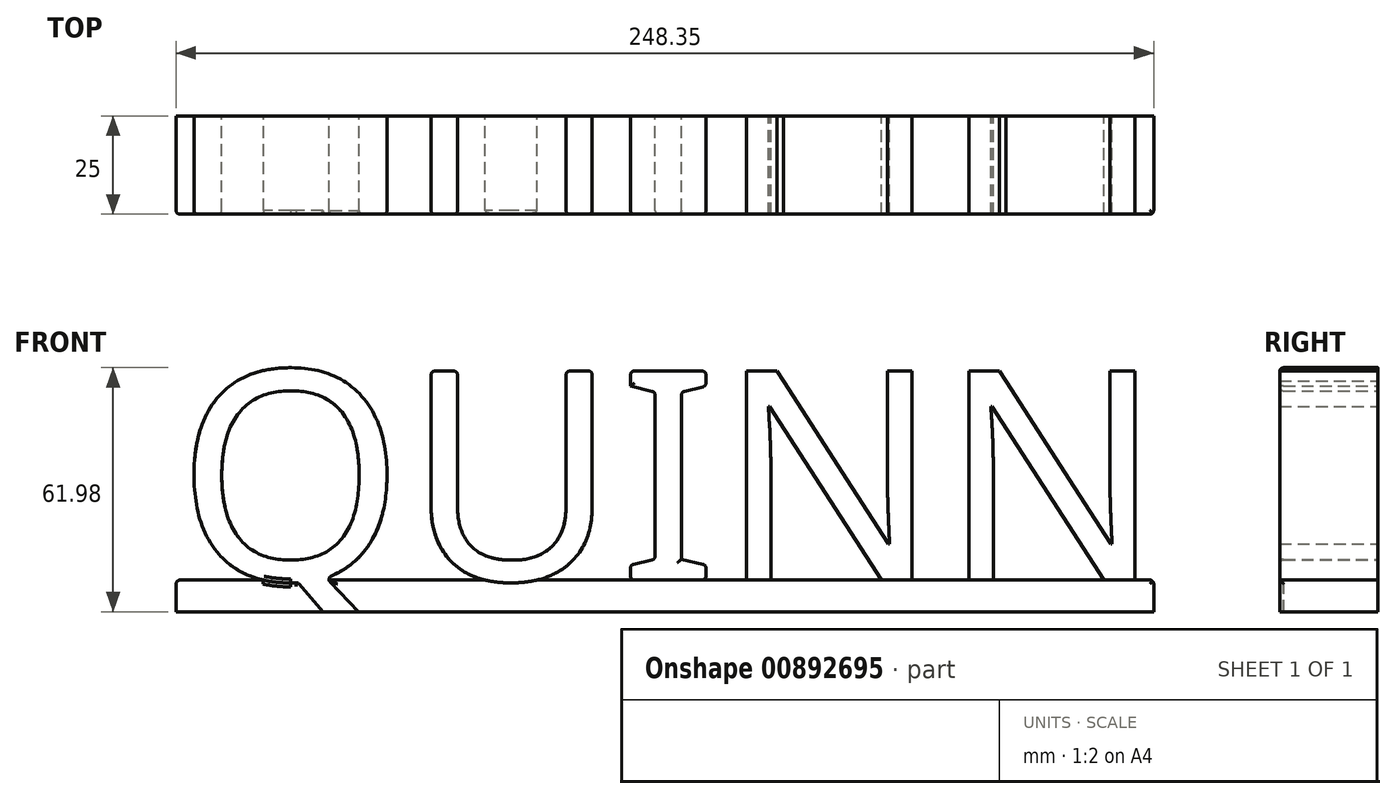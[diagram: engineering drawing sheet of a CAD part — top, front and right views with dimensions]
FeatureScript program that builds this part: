
annotation { "Feature Type Name" : "Feature", "Feature Type Description" : "" }
export const myFeature = defineFeature(function(context is Context, id is Id, definition is map)
    precondition{}
    {
        {
            var Q0;
            Q0=qCreatedBy(makeId("Front.planeOp"),FACE);
            var sketch = newSketch(context, id + "F0", { "sketchPlane" : qUnion([Q0])});
            skText(sketch, "E0", { "text": "QUINN", "fontName": "NotoSans-Regular.ttf"});
            skLineSegment(sketch, "E1.bottom", {"start": v(-74, 3.83) * mm, "end": v(174.35, 3.83) * mm});
            skLineSegment(sketch, "E1.top", {"start": v(-74, -4.21) * mm, "end": v(174.35, -4.21) * mm});
            skLineSegment(sketch, "E1.left", {"start": v(-74, 3.83) * mm, "end": v(-74, -4.21) * mm});
            skLineSegment(sketch, "E1.right", {"start": v(174.35, 3.83) * mm, "end": v(174.35, -4.21) * mm});
            const initialGuessF0  = {"E0": [-0.074, 0.00383, 1, 0, 0.05356]};
            skSetInitialGuess(sketch, initialGuessF0);
            skSolve(sketch);
        }
        {
            var Q0;
            {var subQ1=sQuery(id+"F0.wireOp",EDGE,"E0.sketch_text.stroke-65");Q0=makeQuery(id+"F0.imprint","IMPRINT",FACE,{"disambiguationData":[TD([[makeQuery(id+"F0.imprint","IMPRINT",EDGE,{"derivedFrom":subQ1}),-1.0]])]});}
            var Q1;
            {var subQ2=sQuery(id+"F0.wireOp",EDGE,"E0.sketch_text.stroke-47");Q1=makeQuery(id+"F0.imprint","IMPRINT",FACE,{"disambiguationData":[TD([[makeQuery(id+"F0.imprint","IMPRINT",EDGE,{"derivedFrom":subQ2}),-1.0]])]});}
            var Q2;
            {var subQ0=sQuery(id+"F0.wireOp",EDGE,"E0.sketch_text.stroke-35");Q2=makeQuery(id+"F0.imprint","IMPRINT",FACE,{"disambiguationData":[TD([[makeQuery(id+"F0.imprint","IMPRINT",EDGE,{"derivedFrom":subQ0}),-1.0]])]});}
            var Q3;
            Q3=makeQuery(id+"F0.imprint","IMPRINT",FACE,{"disambiguationData":[TD([[makeQuery(id+"F0.imprint","IMPRINT",EDGE,{"derivedFrom":sQuery(id+"F0.wireOp",EDGE,"E0.sketch_text.stroke-20")}),-1.0]])]});
            var Q4;
            Q4=makeQuery(id+"F0.imprint","IMPRINT",FACE,{"disambiguationData":[TD([[makeQuery(id+"F0.imprint","IMPRINT",EDGE,{"derivedFrom":sQuery(id+"F0.wireOp",EDGE,"E0.sketch_text.stroke-0")}),-1.0]])]});
            var Q5;
            {var subQ1=sQuery(id+"F0.wireOp",EDGE,"E0.sketch_text.stroke-5");Q5=makeQuery(id+"F0.imprint","IMPRINT",FACE,{"disambiguationData":[TD([[makeQuery(id+"F0.imprint","IMPRINT",EDGE,{"derivedFrom":subQ1}),-1.0]])]});}
            var Q6;
            {var subQ0=sQuery(id+"F0.wireOp",EDGE,"E0.sketch_text.stroke-23");var subQ1=sQuery(id+"F0.wireOp",EDGE,"E0.sketch_text.stroke-22");var subQ2=makeQuery(id+"F0.imprint","INTERSECT",VERTEX,{"derivedFrom":[subQ1,subQ0]});Q6=makeQuery(id+"F0.imprint","IMPRINT",FACE,{"disambiguationData":[TD([[makeQuery(id+"F0.imprint","IMPRINT",EDGE,{"disambiguationData":[TD([[subQ2,1.0]])],"derivedFrom":subQ1}),-1.0]])]});}
            extrude(context, id + "F1", {"entities" : qUnion([Q0, Q1, Q2, Q3, Q4, Q5, Q6]), "depth" : 25 * mm, "offsetDistance" : 25 * mm});
        }
        {
            var Q0;
            Q0=makeQuery(id+"F1.opExtrude","CAP_EDGE",EDGE,{"disambiguationData":[OSD([sQuery(id+"F0.wireOp",EDGE,"E0.sketch_text.stroke-7")])],"isStart":false});
            var Q1;
            Q1=makeQuery(id+"F1.opExtrude","CAP_EDGE",EDGE,{"disambiguationData":[OSD([sQuery(id+"F0.wireOp",EDGE,"E0.sketch_text.stroke-14")])],"isStart":false});
            var Q2;
            Q2=makeQuery(id+"F1.opExtrude","CAP_EDGE",EDGE,{"disambiguationData":[OSD([sQuery(id+"F0.wireOp",EDGE,"E0.sketch_text.stroke-2")])],"isStart":false});
            var Q3;
            Q3=makeQuery(id+"F1.opExtrude","CAP_EDGE",EDGE,{"disambiguationData":[OSD([sQuery(id+"F0.wireOp",EDGE,"E0.sketch_text.stroke-4")])],"isStart":false});
            var Q4;
            Q4=makeQuery(id+"F1.opExtrude","CAP_EDGE",EDGE,{"disambiguationData":[OSD([sQuery(id+"F0.wireOp",EDGE,"E0.sketch_text.stroke-5")])],"isStart":false});
            var Q5;
            Q5=makeQuery(id+"F1.opExtrude","CAP_FACE",FACE,{"disambiguationData":[OSD([sQuery(id+"F0.wireOp",EDGE,"E0.sketch_text.stroke-20"),sQuery(id+"F0.wireOp",EDGE,"E0.sketch_text.stroke-21"),sQuery(id+"F0.wireOp",EDGE,"E0.sketch_text.stroke-22"),sQuery(id+"F0.wireOp",EDGE,"E0.sketch_text.stroke-23"),sQuery(id+"F0.wireOp",EDGE,"E0.sketch_text.stroke-24"),sQuery(id+"F0.wireOp",EDGE,"E0.sketch_text.stroke-25"),sQuery(id+"F0.wireOp",EDGE,"E0.sketch_text.stroke-26"),sQuery(id+"F0.wireOp",EDGE,"E0.sketch_text.stroke-27"),sQuery(id+"F0.wireOp",EDGE,"E0.sketch_text.stroke-28"),sQuery(id+"F0.wireOp",EDGE,"E0.sketch_text.stroke-29"),sQuery(id+"F0.wireOp",EDGE,"E0.sketch_text.stroke-30"),sQuery(id+"F0.wireOp",EDGE,"E0.sketch_text.stroke-31"),sQuery(id+"F0.wireOp",EDGE,"E0.sketch_text.stroke-32"),sQuery(id+"F0.wireOp",EDGE,"E0.sketch_text.stroke-33"),sQuery(id+"F0.wireOp",EDGE,"E1.bottom")])],"isStart":false});
            var Q6;
            Q6=makeQuery(id+"F1.opExtrude","CAP_FACE",FACE,{"disambiguationData":[OSD([sQuery(id+"F0.wireOp",EDGE,"E0.sketch_text.stroke-35"),sQuery(id+"F0.wireOp",EDGE,"E0.sketch_text.stroke-36"),sQuery(id+"F0.wireOp",EDGE,"E0.sketch_text.stroke-37"),sQuery(id+"F0.wireOp",EDGE,"E0.sketch_text.stroke-38"),sQuery(id+"F0.wireOp",EDGE,"E0.sketch_text.stroke-39"),sQuery(id+"F0.wireOp",EDGE,"E0.sketch_text.stroke-40"),sQuery(id+"F0.wireOp",EDGE,"E0.sketch_text.stroke-41"),sQuery(id+"F0.wireOp",EDGE,"E0.sketch_text.stroke-42"),sQuery(id+"F0.wireOp",EDGE,"E0.sketch_text.stroke-43"),sQuery(id+"F0.wireOp",EDGE,"E0.sketch_text.stroke-44"),sQuery(id+"F0.wireOp",EDGE,"E0.sketch_text.stroke-45"),sQuery(id+"F0.wireOp",EDGE,"E1.bottom")])],"isStart":false});
            var Q7;
            Q7=makeQuery(id+"F1.opExtrude","CAP_FACE",FACE,{"disambiguationData":[OSD([sQuery(id+"F0.wireOp",EDGE,"E0.sketch_text.stroke-47"),sQuery(id+"F0.wireOp",EDGE,"E0.sketch_text.stroke-48"),sQuery(id+"F0.wireOp",EDGE,"E0.sketch_text.stroke-49"),sQuery(id+"F0.wireOp",EDGE,"E0.sketch_text.stroke-50"),sQuery(id+"F0.wireOp",EDGE,"E0.sketch_text.stroke-51"),sQuery(id+"F0.wireOp",EDGE,"E0.sketch_text.stroke-53"),sQuery(id+"F0.wireOp",EDGE,"E0.sketch_text.stroke-54"),sQuery(id+"F0.wireOp",EDGE,"E0.sketch_text.stroke-55"),sQuery(id+"F0.wireOp",EDGE,"E0.sketch_text.stroke-56"),sQuery(id+"F0.wireOp",EDGE,"E0.sketch_text.stroke-57"),sQuery(id+"F0.wireOp",EDGE,"E0.sketch_text.stroke-58"),sQuery(id+"F0.wireOp",EDGE,"E0.sketch_text.stroke-59"),sQuery(id+"F0.wireOp",EDGE,"E0.sketch_text.stroke-60"),sQuery(id+"F0.wireOp",EDGE,"E0.sketch_text.stroke-61"),sQuery(id+"F0.wireOp",EDGE,"E0.sketch_text.stroke-62"),sQuery(id+"F0.wireOp",EDGE,"E0.sketch_text.stroke-63"),sQuery(id+"F0.wireOp",EDGE,"E1.bottom")])],"isStart":false});
            var Q8;
            Q8=makeQuery(id+"F1.opExtrude","CAP_FACE",FACE,{"disambiguationData":[OSD([sQuery(id+"F0.wireOp",EDGE,"E0.sketch_text.stroke-65"),sQuery(id+"F0.wireOp",EDGE,"E0.sketch_text.stroke-66"),sQuery(id+"F0.wireOp",EDGE,"E0.sketch_text.stroke-67"),sQuery(id+"F0.wireOp",EDGE,"E0.sketch_text.stroke-68"),sQuery(id+"F0.wireOp",EDGE,"E0.sketch_text.stroke-69"),sQuery(id+"F0.wireOp",EDGE,"E0.sketch_text.stroke-71"),sQuery(id+"F0.wireOp",EDGE,"E0.sketch_text.stroke-72"),sQuery(id+"F0.wireOp",EDGE,"E0.sketch_text.stroke-73"),sQuery(id+"F0.wireOp",EDGE,"E0.sketch_text.stroke-74"),sQuery(id+"F0.wireOp",EDGE,"E0.sketch_text.stroke-75"),sQuery(id+"F0.wireOp",EDGE,"E0.sketch_text.stroke-76"),sQuery(id+"F0.wireOp",EDGE,"E0.sketch_text.stroke-77"),sQuery(id+"F0.wireOp",EDGE,"E0.sketch_text.stroke-78"),sQuery(id+"F0.wireOp",EDGE,"E0.sketch_text.stroke-79"),sQuery(id+"F0.wireOp",EDGE,"E0.sketch_text.stroke-80"),sQuery(id+"F0.wireOp",EDGE,"E0.sketch_text.stroke-81"),sQuery(id+"F0.wireOp",EDGE,"E1.bottom")])],"isStart":false});
            var Q9;
            Q9=makeQuery(id+"F1.opExtrude","SWEPT_EDGE",EDGE,{"disambiguationData":[OSD([sQuery(id+"F0.wireOp",EDGE,"E0.sketch_text.stroke-1"),sQuery(id+"F0.wireOp",EDGE,"E0.sketch_text.stroke-2")])]});
            var Q10;
            Q10=makeQuery(id+"F1.opExtrude","SWEPT_EDGE",EDGE,{"disambiguationData":[OSD([sQuery(id+"F0.wireOp",EDGE,"E0.sketch_text.stroke-4"),sQuery(id+"F0.wireOp",EDGE,"E0.sketch_text.stroke-5")])]});
            var Q11;
            Q11=makeQuery(id+"F1.opExtrude","SWEPT_EDGE",EDGE,{"disambiguationData":[OSD([sQuery(id+"F0.wireOp",EDGE,"E0.sketch_text.stroke-25"),sQuery(id+"F0.wireOp",EDGE,"E0.sketch_text.stroke-26")])]});
            var Q12;
            Q12=makeQuery(id+"F1.opExtrude","SWEPT_EDGE",EDGE,{"disambiguationData":[OSD([sQuery(id+"F0.wireOp",EDGE,"E0.sketch_text.stroke-26"),sQuery(id+"F0.wireOp",EDGE,"E0.sketch_text.stroke-27")])]});
            var Q13;
            Q13=makeQuery(id+"F1.opExtrude","SWEPT_EDGE",EDGE,{"disambiguationData":[OSD([sQuery(id+"F0.wireOp",EDGE,"E0.sketch_text.stroke-32"),sQuery(id+"F0.wireOp",EDGE,"E0.sketch_text.stroke-33")])]});
            var Q14;
            Q14=makeQuery(id+"F1.opExtrude","SWEPT_EDGE",EDGE,{"disambiguationData":[OSD([sQuery(id+"F0.wireOp",EDGE,"E0.sketch_text.stroke-20"),sQuery(id+"F0.wireOp",EDGE,"E0.sketch_text.stroke-33")])]});
            var Q15;
            Q15=makeQuery(id+"F1.opExtrude","SWEPT_EDGE",EDGE,{"disambiguationData":[OSD([sQuery(id+"F0.wireOp",EDGE,"E0.sketch_text.stroke-39"),sQuery(id+"F0.wireOp",EDGE,"E0.sketch_text.stroke-40")])]});
            var Q16;
            Q16=makeQuery(id+"F1.opExtrude","SWEPT_EDGE",EDGE,{"disambiguationData":[OSD([sQuery(id+"F0.wireOp",EDGE,"E0.sketch_text.stroke-40"),sQuery(id+"F0.wireOp",EDGE,"E0.sketch_text.stroke-41")])]});
            var Q17;
            Q17=makeQuery(id+"F1.opExtrude","SWEPT_EDGE",EDGE,{"disambiguationData":[OSD([sQuery(id+"F0.wireOp",EDGE,"E0.sketch_text.stroke-41"),sQuery(id+"F0.wireOp",EDGE,"E0.sketch_text.stroke-42")])]});
            var Q18;
            Q18=makeQuery(id+"F1.opExtrude","SWEPT_EDGE",EDGE,{"disambiguationData":[OSD([sQuery(id+"F0.wireOp",EDGE,"E0.sketch_text.stroke-42"),sQuery(id+"F0.wireOp",EDGE,"E0.sketch_text.stroke-43")])]});
            var Q19;
            Q19=makeQuery(id+"F1.opExtrude","SWEPT_EDGE",EDGE,{"disambiguationData":[OSD([sQuery(id+"F0.wireOp",EDGE,"E0.sketch_text.stroke-37"),sQuery(id+"F0.wireOp",EDGE,"E0.sketch_text.stroke-38")])]});
            var Q20;
            Q20=makeQuery(id+"F1.opExtrude","SWEPT_EDGE",EDGE,{"disambiguationData":[OSD([sQuery(id+"F0.wireOp",EDGE,"E0.sketch_text.stroke-36"),sQuery(id+"F0.wireOp",EDGE,"E0.sketch_text.stroke-37")])]});
            var Q21;
            Q21=makeQuery(id+"F1.opExtrude","SWEPT_EDGE",EDGE,{"disambiguationData":[OSD([sQuery(id+"F0.wireOp",EDGE,"E0.sketch_text.stroke-35"),sQuery(id+"F0.wireOp",EDGE,"E0.sketch_text.stroke-36")])]});
            var Q22;
            Q22=makeQuery(id+"F1.opExtrude","SWEPT_EDGE",EDGE,{"disambiguationData":[OSD([sQuery(id+"F0.wireOp",EDGE,"E0.sketch_text.stroke-35"),sQuery(id+"F0.wireOp",EDGE,"E1.bottom")])]});
            var Q23;
            Q23=makeQuery(id+"F1.opExtrude","SWEPT_EDGE",EDGE,{"disambiguationData":[OSD([sQuery(id+"F0.wireOp",EDGE,"E0.sketch_text.stroke-45"),sQuery(id+"F0.wireOp",EDGE,"E1.bottom")])]});
            var Q24;
            Q24=makeQuery(id+"F1.opExtrude","SWEPT_EDGE",EDGE,{"disambiguationData":[OSD([sQuery(id+"F0.wireOp",EDGE,"E0.sketch_text.stroke-44"),sQuery(id+"F0.wireOp",EDGE,"E0.sketch_text.stroke-45")])]});
            var Q25;
            Q25=makeQuery(id+"F1.opExtrude","SWEPT_EDGE",EDGE,{"disambiguationData":[OSD([sQuery(id+"F0.wireOp",EDGE,"E0.sketch_text.stroke-53"),sQuery(id+"F0.wireOp",EDGE,"E1.bottom")])]});
            var Q26;
            Q26=makeQuery(id+"F1.opExtrude","SWEPT_EDGE",EDGE,{"disambiguationData":[OSD([sQuery(id+"F0.wireOp",EDGE,"E0.sketch_text.stroke-53"),sQuery(id+"F0.wireOp",EDGE,"E0.sketch_text.stroke-54")])]});
            var Q27;
            Q27=makeQuery(id+"F1.opExtrude","SWEPT_EDGE",EDGE,{"disambiguationData":[OSD([sQuery(id+"F0.wireOp",EDGE,"E0.sketch_text.stroke-54"),sQuery(id+"F0.wireOp",EDGE,"E0.sketch_text.stroke-55")])]});
            var Q28;
            Q28=makeQuery(id+"F1.opExtrude","SWEPT_EDGE",EDGE,{"disambiguationData":[OSD([sQuery(id+"F0.wireOp",EDGE,"E0.sketch_text.stroke-61"),sQuery(id+"F0.wireOp",EDGE,"E0.sketch_text.stroke-62")])]});
            var Q29;
            Q29=makeQuery(id+"F1.opExtrude","SWEPT_EDGE",EDGE,{"disambiguationData":[OSD([sQuery(id+"F0.wireOp",EDGE,"E0.sketch_text.stroke-62"),sQuery(id+"F0.wireOp",EDGE,"E0.sketch_text.stroke-63")])]});
            var Q30;
            Q30=makeQuery(id+"F1.opExtrude","SWEPT_EDGE",EDGE,{"disambiguationData":[OSD([sQuery(id+"F0.wireOp",EDGE,"E0.sketch_text.stroke-63"),sQuery(id+"F0.wireOp",EDGE,"E1.bottom")])]});
            var Q31;
            Q31=makeQuery(id+"F1.opExtrude","SWEPT_EDGE",EDGE,{"disambiguationData":[OSD([sQuery(id+"F0.wireOp",EDGE,"E0.sketch_text.stroke-47"),sQuery(id+"F0.wireOp",EDGE,"E1.bottom")])]});
            var Q32;
            Q32=makeQuery(id+"F1.opExtrude","SWEPT_EDGE",EDGE,{"disambiguationData":[OSD([sQuery(id+"F0.wireOp",EDGE,"E0.sketch_text.stroke-51"),sQuery(id+"F0.wireOp",EDGE,"E1.bottom")])]});
            var Q33;
            Q33=makeQuery(id+"F1.opExtrude","SWEPT_EDGE",EDGE,{"disambiguationData":[OSD([sQuery(id+"F0.wireOp",EDGE,"E0.sketch_text.stroke-71"),sQuery(id+"F0.wireOp",EDGE,"E0.sketch_text.stroke-72")])]});
            var Q34;
            Q34=makeQuery(id+"F1.opExtrude","SWEPT_EDGE",EDGE,{"disambiguationData":[OSD([sQuery(id+"F0.wireOp",EDGE,"E0.sketch_text.stroke-72"),sQuery(id+"F0.wireOp",EDGE,"E0.sketch_text.stroke-73")])]});
            var Q35;
            Q35=makeQuery(id+"F1.opExtrude","SWEPT_EDGE",EDGE,{"disambiguationData":[OSD([sQuery(id+"F0.wireOp",EDGE,"E0.sketch_text.stroke-79"),sQuery(id+"F0.wireOp",EDGE,"E0.sketch_text.stroke-80")])]});
            var Q36;
            Q36=makeQuery(id+"F1.opExtrude","SWEPT_EDGE",EDGE,{"disambiguationData":[OSD([sQuery(id+"F0.wireOp",EDGE,"E0.sketch_text.stroke-80"),sQuery(id+"F0.wireOp",EDGE,"E0.sketch_text.stroke-81")])]});
            var Q37;
            Q37=makeQuery(id+"F1.opExtrude","SWEPT_EDGE",EDGE,{"disambiguationData":[OSD([sQuery(id+"F0.wireOp",EDGE,"E0.sketch_text.stroke-81"),sQuery(id+"F0.wireOp",EDGE,"E1.bottom")])]});
            var Q38;
            Q38=makeQuery(id+"F1.opExtrude","SWEPT_EDGE",EDGE,{"disambiguationData":[OSD([sQuery(id+"F0.wireOp",EDGE,"E0.sketch_text.stroke-65"),sQuery(id+"F0.wireOp",EDGE,"E1.bottom")])]});
            var Q39;
            Q39=makeQuery(id+"F1.opExtrude","SWEPT_EDGE",EDGE,{"disambiguationData":[OSD([sQuery(id+"F0.wireOp",EDGE,"E0.sketch_text.stroke-69"),sQuery(id+"F0.wireOp",EDGE,"E1.bottom")])]});
            var Q40;
            Q40=makeQuery(id+"F1.opExtrude","SWEPT_EDGE",EDGE,{"disambiguationData":[OSD([sQuery(id+"F0.wireOp",EDGE,"E0.sketch_text.stroke-71"),sQuery(id+"F0.wireOp",EDGE,"E1.bottom")])]});
            fillet(context, id + "F2", {"entities" : qUnion([Q0, Q1, Q2, Q3, Q4, Q5, Q6, Q7, Q8, Q9, Q10, Q11, Q12, Q13, Q14, Q15, Q16, Q17, Q18, Q19, Q20, Q21, Q22, Q23, Q24, Q25, Q26, Q27, Q28, Q29, Q30, Q31, Q32, Q33, Q34, Q35, Q36, Q37, Q38, Q39, Q40]), "tangentPropagation" : true, "radius" : 1 * mm, "defaultsChanged" : false, "vertexSettings" : [], "allowEdgeOverflow" : false});
        }
        {
            var Q0;
            {var subQ1=sQuery(id+"F0.wireOp",EDGE,"E0.sketch_text.stroke-5");Q0=makeQuery(id+"F0.imprint","IMPRINT",FACE,{"disambiguationData":[TD([[makeQuery(id+"F0.imprint","IMPRINT",EDGE,{"derivedFrom":subQ1}),1.0]])]});}
            var Q1;
            {var subQ19=sQuery(id+"F0.wireOp",EDGE,"E1.right");Q1=makeQuery(id+"F0.imprint","IMPRINT",FACE,{"disambiguationData":[TD([[makeQuery(id+"F0.imprint","IMPRINT",EDGE,{"derivedFrom":subQ19}),-1.0]])]});}
            extrude(context, id + "F3", {"entities" : qUnion([Q0, Q1]), "operationType" : NewBodyOperationType.ADD, "depth" : 25 * mm, "offsetDistance" : 25 * mm});
        }
        {
            var Q0;
            {var subQ0=sQuery(id+"F0.wireOp",EDGE,"E1.bottom");Q0=makeQuery(id+"F3.opExtrude","CAP_EDGE",EDGE,{"disambiguationData":[OSD([subQ0]),TDD([makeQuery(id+"F0.imprint","IMPRINT",EDGE,{"disambiguationData":[TD([[makeQuery(id+"F0.imprint","INTERSECT",VERTEX,{"derivedFrom":[subQ0,sQuery(id+"F0.wireOp",EDGE,"E1.left")]}),-1.0]])],"derivedFrom":subQ0})])],"isStart":false});}
            var Q1;
            {var subQ0=sQuery(id+"F0.wireOp",EDGE,"E1.bottom");Q1=makeQuery(id+"F3.opExtrude","CAP_EDGE",EDGE,{"disambiguationData":[OSD([subQ0]),TDD([makeQuery(id+"F0.imprint","IMPRINT",EDGE,{"disambiguationData":[TD([[makeQuery(id+"F0.imprint","INTERSECT",VERTEX,{"derivedFrom":[sQuery(id+"F0.wireOp",EDGE,"E0.sketch_text.stroke-2"),subQ0]}),-1.0]])],"derivedFrom":subQ0})])],"isStart":false});}
            var Q2;
            Q2=makeQuery(id+"F3.opExtrude","CAP_EDGE",EDGE,{"disambiguationData":[OSD([sQuery(id+"F0.wireOp",EDGE,"E0.sketch_text.stroke-2")])],"isStart":false});
            var Q3;
            Q3=makeQuery(id+"F3.opExtrude","CAP_EDGE",EDGE,{"disambiguationData":[OSD([sQuery(id+"F0.wireOp",EDGE,"E0.sketch_text.stroke-5")])],"isStart":false});
            var Q4;
            Q4=makeQuery(id+"F3.opExtrude","SWEPT_EDGE",EDGE,{"disambiguationData":[OSD([sQuery(id+"F0.wireOp",EDGE,"E0.sketch_text.stroke-4"),sQuery(id+"F0.wireOp",EDGE,"E0.sketch_text.stroke-5")])]});
            var Q5;
            Q5=makeQuery(id+"F3.opExtrude","CAP_EDGE",EDGE,{"disambiguationData":[OSD([sQuery(id+"F0.wireOp",EDGE,"E0.sketch_text.stroke-4")])],"isStart":false});
            var Q6;
            Q6=makeQuery(id+"F3.opExtrude","CAP_EDGE",EDGE,{"disambiguationData":[OSD([sQuery(id+"F0.wireOp",EDGE,"E1.right")])],"isStart":false});
            var Q7;
            Q7=makeQuery(id+"F3.opExtrude","SWEPT_EDGE",EDGE,{"disambiguationData":[OSD([sQuery(id+"F0.wireOp",EDGE,"E1.bottom"),sQuery(id+"F0.wireOp",EDGE,"E1.right")])]});
            var Q8;
            Q8=makeQuery(id+"F3.opExtrude","SWEPT_EDGE",EDGE,{"disambiguationData":[OSD([sQuery(id+"F0.wireOp",EDGE,"E1.bottom"),sQuery(id+"F0.wireOp",EDGE,"E1.left")])]});
            var Q9;
            Q9=makeQuery(id+"F3.opExtrude","CAP_EDGE",EDGE,{"disambiguationData":[OSD([sQuery(id+"F0.wireOp",EDGE,"E1.left")])],"isStart":false});
            fillet(context, id + "F4", {"entities" : qUnion([Q0, Q1, Q2, Q3, Q4, Q5, Q6, Q7, Q8, Q9]), "tangentPropagation" : true, "radius" : 1 * mm, "defaultsChanged" : false, "vertexSettings" : [], "allowEdgeOverflow" : false});
        }
    });
